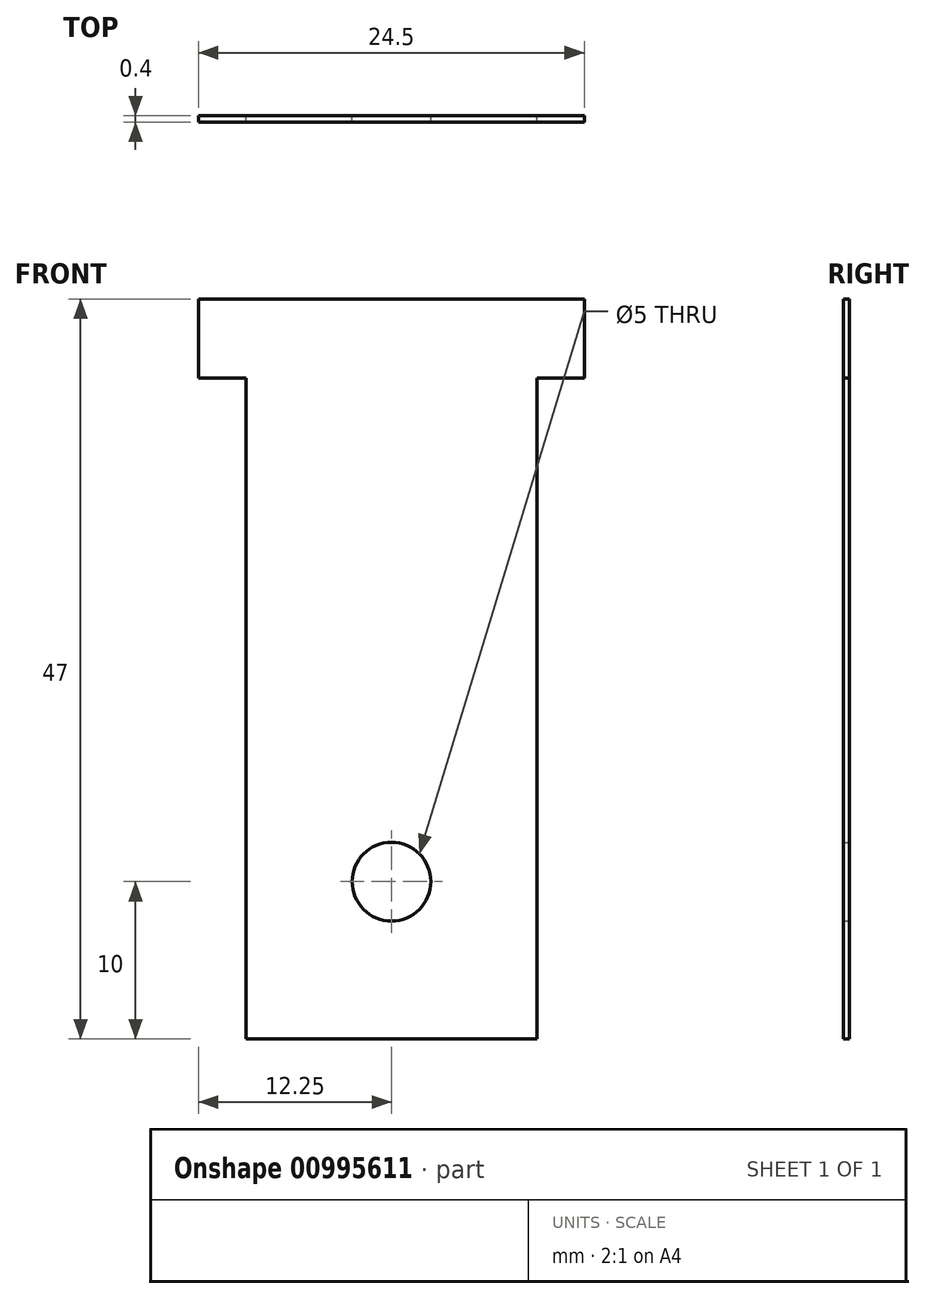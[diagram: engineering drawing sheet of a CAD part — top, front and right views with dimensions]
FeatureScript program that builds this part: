
annotation { "Feature Type Name" : "Feature", "Feature Type Description" : "" }
export const myFeature = defineFeature(function(context is Context, id is Id, definition is map)
    precondition{}
    {
        {
            var Q0;
            Q0=qCreatedBy(makeId("Front.planeOp"),FACE);
            var sketch = newSketch(context, id + "F0", { "sketchPlane" : qUnion([Q0])});
            skLineSegment(sketch, "E0", {"start": v(0, 0) * mm, "end": v(-9.25, 0) * mm});
            skLineSegment(sketch, "E1", {"start": v(-9.25, 0) * mm, "end": v(-9.25, 42) * mm});
            skLineSegment(sketch, "E2", {"start": v(-9.25, 42) * mm, "end": v(-12.25, 42) * mm});
            skLineSegment(sketch, "E3", {"start": v(-12.25, 42) * mm, "end": v(-12.25, 47) * mm});
            skLineSegment(sketch, "E4", {"start": v(-12.25, 47) * mm, "end": v(0, 47) * mm});
            skLineSegment(sketch, "E5.MirrorCS", {"start": v(9.25, 0) * mm, "end": v(9.25, 42) * mm});
            skLineSegment(sketch, "E6.MirrorCS", {"start": v(12.25, 42) * mm, "end": v(12.25, 47) * mm});
            skLineSegment(sketch, "E7.MirrorCS", {"start": v(12.25, 47) * mm, "end": v(0, 47) * mm});
            skLineSegment(sketch, "E8.MirrorCS", {"start": v(0, 0) * mm, "end": v(9.25, 0) * mm});
            skLineSegment(sketch, "E9.MirrorCS", {"start": v(9.25, 42) * mm, "end": v(12.25, 42) * mm});
            skCircle(sketch, "E10", {"center": v(0, 10) * mm, "radius": 2.5 * mm});
            skSolve(sketch);
        }
        {
            var Q0;
            Q0 = qSketchRegion(id + "F0", true);
            extrude(context, id + "F1", {"entities" : qUnion([Q0]), "depth" : 0.4 * mm, "offsetDistance" : 25 * mm});
        }
    });
